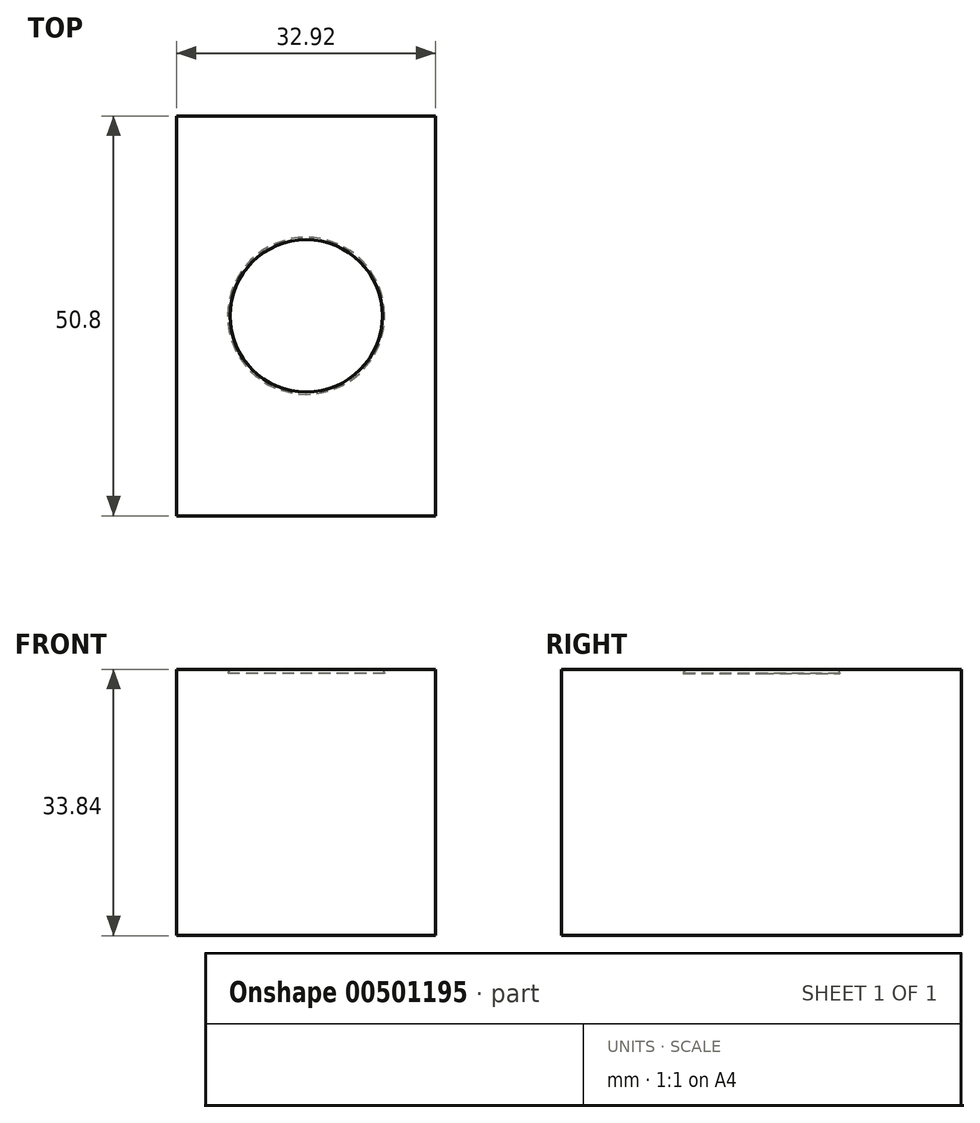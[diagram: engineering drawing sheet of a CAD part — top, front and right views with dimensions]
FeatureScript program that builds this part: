
annotation { "Feature Type Name" : "Feature", "Feature Type Description" : "" }
export const myFeature = defineFeature(function(context is Context, id is Id, definition is map)
    precondition{}
    {
        {
            var Q0;
            Q0=qCreatedBy(makeId("Front.planeOp"),FACE);
            var sketch = newSketch(context, id + "F0", { "sketchPlane" : qUnion([Q0])});
            skLineSegment(sketch, "E0.bottom", {"start": v(-16.46, 16.92) * mm, "end": v(16.46, 16.92) * mm});
            skLineSegment(sketch, "E0.top", {"start": v(-16.46, -16.92) * mm, "end": v(16.46, -16.92) * mm});
            skLineSegment(sketch, "E0.left", {"start": v(-16.46, 16.92) * mm, "end": v(-16.46, -16.92) * mm});
            skLineSegment(sketch, "E0.right", {"start": v(16.46, 16.92) * mm, "end": v(16.46, -16.92) * mm});
            skPoint(sketch, "E0.middle", {"position": v(0, 0) * mm});
            skSolve(sketch);
        }
        {
            var Q0;
            Q0=makeQuery(id+"F0.imprint","IMPRINT",FACE,{"disambiguationData":[TD([[makeQuery(id+"F0.imprint","IMPRINT",EDGE,{"derivedFrom":sQuery(id+"F0.wireOp",EDGE,"E0.bottom")}),-1.0]])]});
            extrude(context, id + "F1", {"entities" : qUnion([Q0]), "endBound" : BoundingType.SYMMETRIC, "depth" : 50.8 * mm});
        }
        {
            var Q0;
            Q0=makeQuery(id+"F1.opExtrude","SWEPT_FACE",FACE,{"disambiguationData":[OSD([sQuery(id+"F0.wireOp",EDGE,"E0.bottom")])]});
            var sketch = newSketch(context, id + "F2", { "sketchPlane" : qUnion([Q0])});
            skCircle(sketch, "E1", {"center": v(0, 0) * mm, "radius": 9.68 * mm});
            skSolve(sketch);
        }
        {
            var Q0;
            Q0 = qSketchRegion(id + "F2", true);
            extrude(context, id + "F3", {"entities" : qUnion([Q0]), "operationType" : NewBodyOperationType.REMOVE, "oppositeDirection" : true, "depth" : 0.5 * mm, "hasDraft" : true, "draftAngle" : 30 * degree});
        }
    });
